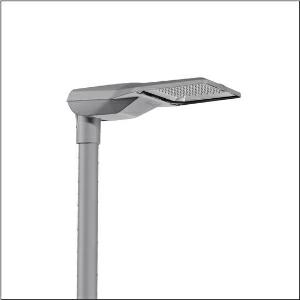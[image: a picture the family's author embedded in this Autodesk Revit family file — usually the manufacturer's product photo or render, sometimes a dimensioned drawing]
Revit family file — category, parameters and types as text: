
# Revit family: streetlight_sl_21_midi___st1_0ab_5xe7m33a08lb_7eb4
name_source: partatom
category: Lighting Fixtures
units: mm (PartAtom-declared; Revit-internal decimal feet)

## family parameters
Cut with Voids When Loaded = No
Host = Face
Light Source = No
Part Type = Normal
Room Calculation Point = No
Round Connector Dimension = Use Diameter
Shared = No

## types (1)
- --- (1 x LED, 12620 lm, 98.3 W, 3000K)
    Apparent Load = 98 VA
    CIE Flux Codes = 38 73 97 100 100
    Color Rendering = 70
    Color Temperature = 3000K
    Default Elevation = 1800 mm
    Description = Streetlight SL 21 midi, mast luminaire, primary light control with lens, of PMMA, primary optical cover: cover, of toughened safety glass, transparent, light distribution: ST1.0aB, light emission: direct distribution, primary light characteristic: asymmetric, installation type: post-top, side-entry, LED, 3G 1.5mm², High Power LED, rated luminous flux: 12.620lm, luminous efficacy: 128lm/W, light colour: 730, colour temperature: 3000K, control: flexible luminous flux parameterisation, time-dependent luminous flux control, constant luminous flux control, overheat protection, mains connection: 220..240V, AC, 50/60Hz, connection cable pre-assembled, cable length: 10,5m, wiring characteristics: H07RN-F, start of lifetime: 98W, end of service life: 101W, reduction: 44W, luminaire housing, of diecast aluminium, powder-coated, Siteco® metallic grey (DB 702S), corrosivity category C5 mid according to DIN EN ISO 12944, please order mast flange separately, inclination adjustable: 0°, 5°, 10°, 15°, sealing non-destructively replaceable, multi-level sealing system, length: 644mm, width: 335mm, height: 110mm, mast flange for spigot size: 42mm (side-entry): 5XC10008XM4, 60/48mm (side-entry/post-top): 5XC10108XM2, 76/60mm (side-entry/post-top): 5XC10108XM1, protection rating (complete): IP66, insulation class (complete): insulation class II (safety insulation), certification: CE, ENEC, ENEC+, VDE, impact resistance: IK09, permissible operating ambient temperature for outdoor applications: -40..+50°C, standard-compliant lighting for roads and squares, packaging unit: 1 piece

Light Distribution: ST1.0aB
    Height = 111 mm
    Lamp = 1 x LED
    Lamp Light Flux = 12620 lm
    Lamp Power = 98.3 W
    Lamp count = 1
    Length = 644 mm
    Luminous efficacy = 128 lm/W
    Manufacturer = Siteco
    ModVariant = No
    Model = 5XE7M33A08LB
    Number of Poles = 1
    OnlyDefault = Yes
    Power Factor = 1
    Product Name = Streetlight SL 21 midi | ST1.0aB
    Product group = mast luminaire | pylon top
    ProductGroupID = 6100
    Protection Class = Protection class II
    Protection Degree = IP 66
    RLX_Detail_Level = 1
    RLX_Emergency_Light_Flux = 0 lm
    RLX_Emergency_Type = 0
    RLX_Emergency_Type_DB = No
    RlxData = <blob elided: 90449 chars, md5=3e3e3fed>
    Socket = socket
    Standby Power = 0 W
    System Light Flux = 12620 lm
    System Power = 98 W
    Type Comments = factory setting: luminous flux: 100 % | Output Level: 100 % | 1020 mA
    Type Image = l_1004298.jpg
    URL = http://relux.com
    VarID = @adj_154387
    Voltage = 0 V
    Weight = 0.00 kg
    Width = 336 mm

## geometry (parser evidence)
native form markers: Blend x4, Sweep x11
no freeform markers — native parametric forms only
